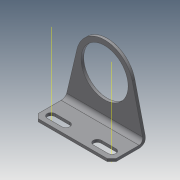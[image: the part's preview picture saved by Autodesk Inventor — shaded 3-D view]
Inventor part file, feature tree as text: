
AUTODESK INVENTOR PART (.ipt)
format: ipt  version: 2020.4 (Build 244396000, 396)  size: 168,960 bytes
history: native  units: in
note: dims shown in document units (in); Inventor stores cm internally (conversion verified against a paired STEP export)
features: other x2, mirror x1, sketch x1, imported_body x1
ambient origin geometry x8: Origin, YZ Plane, XZ Plane, XY Plane, X Axis, Y Axis, Z Axis, Center Point
bodies: Body1 (feature_tree)
feature tree (5):
  mirror  "Mirror1"
  sketch  "Sketch1"  dims[d0=0.41in d1=0.225in d2=1.29in d3=2.175in d4=1.7in d5=1.6875in]
  other  "Work Axis1"
  other  "Work Axis2"
  imported_body  "Base1"
